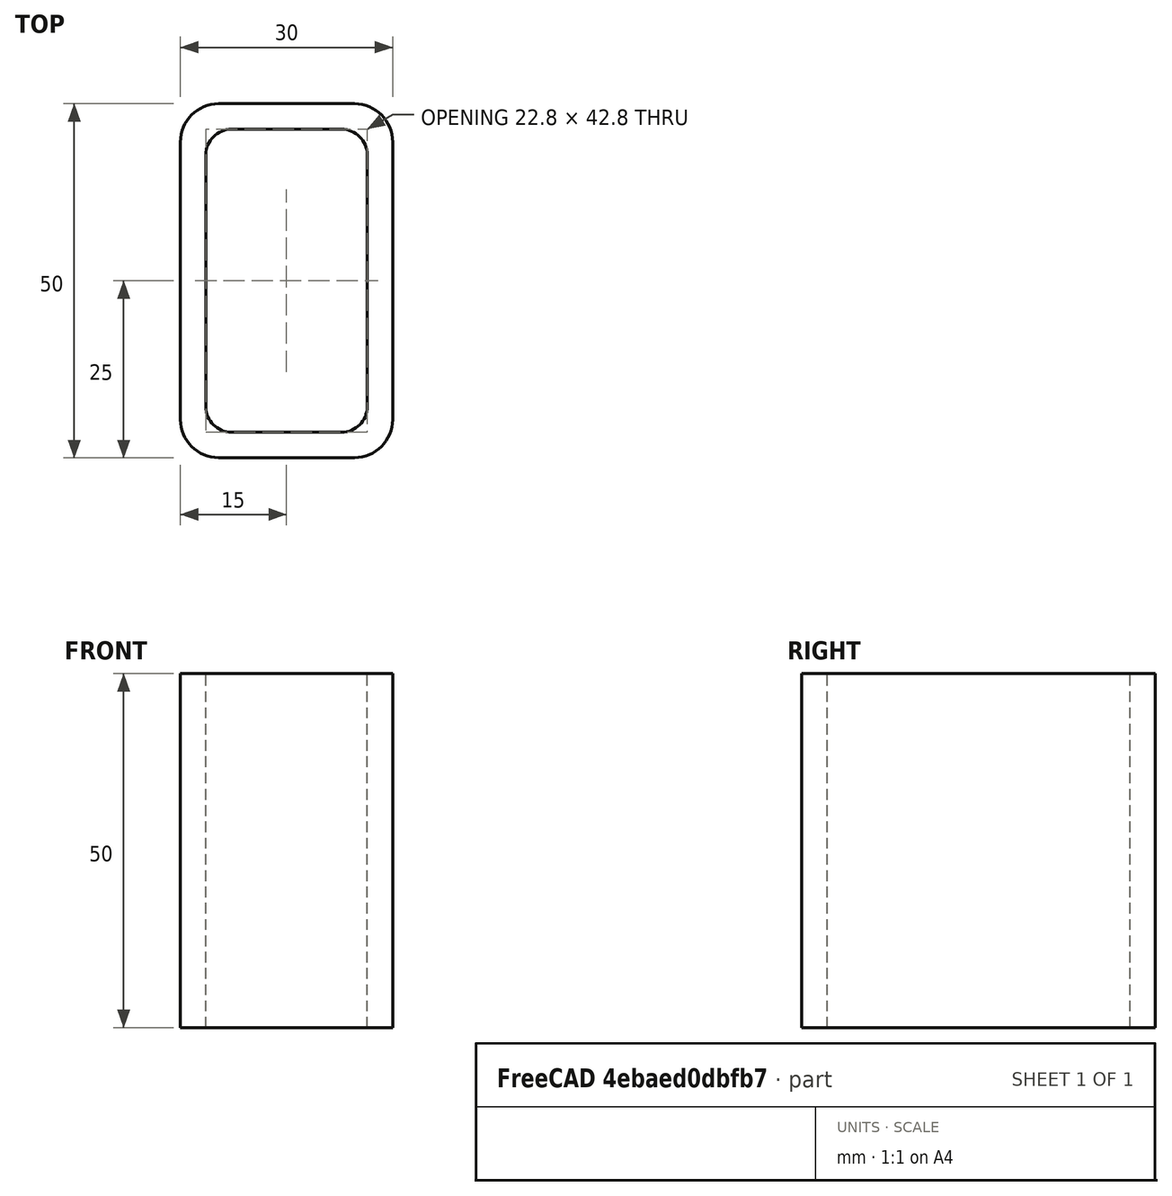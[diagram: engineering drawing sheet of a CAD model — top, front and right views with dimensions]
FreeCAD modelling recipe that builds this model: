
FCSTD DOCUMENT  (FreeCAD 0.15R4671 (Git))
Label: Rectangular hollow section 50x30x3.6 EN10219 S235JRH
License: All rights reserved
LicenseURL: http://en.wikipedia.org/wiki/All_rights_reserved
objects: Sketcher::SketchObject×1, Part::Extrusion×1
note: 2 computed .brp shape members not serialized (recipe doc carries the construction recipe); baked Part::Feature solids carry a one-line shape summary decoded from their .brp

FEATURE [Sketcher::SketchObject] Sketch
  sketch-geometry (16):
    g0: LineSegment StartX=-7.8 StartY=21.4 StartZ=0 EndX=7.8 EndY=21.4 EndZ=0
    g1: LineSegment StartX=11.4 StartY=17.8 StartZ=0 EndX=11.4 EndY=-17.8 EndZ=0
    g2: LineSegment StartX=7.8 StartY=-21.4 StartZ=0 EndX=-7.8 EndY=-21.4 EndZ=0
    g3: LineSegment StartX=-11.4 StartY=-17.8 StartZ=0 EndX=-11.4 EndY=17.8 EndZ=0
    g4: LineSegment StartX=-9.6 StartY=25 StartZ=0 EndX=9.6 EndY=25 EndZ=0
    g5: LineSegment StartX=15 StartY=19.6 StartZ=0 EndX=15 EndY=-19.6 EndZ=0
    g6: LineSegment StartX=9.6 StartY=-25 StartZ=0 EndX=-9.6 EndY=-25 EndZ=0
    g7: LineSegment StartX=-15 StartY=-19.6 StartZ=0 EndX=-15 EndY=19.6 EndZ=0
    g8: ArcOfCircle CenterX=-7.8 CenterY=17.8 CenterZ=0 NormalX=0 NormalY=0 NormalZ=1 Radius=3.6 StartAngle=1.5708 EndAngle=3.14159
    g9: ArcOfCircle CenterX=7.8 CenterY=17.8 CenterZ=0 NormalX=0 NormalY=0 NormalZ=1 Radius=3.6 StartAngle=0 EndAngle=1.5708
    g10: ArcOfCircle CenterX=7.8 CenterY=-17.8 CenterZ=0 NormalX=0 NormalY=0 NormalZ=1 Radius=3.6 StartAngle=4.71239 EndAngle=6.28319
    g11: ArcOfCircle CenterX=-7.8 CenterY=-17.8 CenterZ=0 NormalX=0 NormalY=0 NormalZ=1 Radius=3.6 StartAngle=3.14159 EndAngle=4.71239
    g12: ArcOfCircle CenterX=9.6 CenterY=19.6 CenterZ=0 NormalX=0 NormalY=0 NormalZ=1 Radius=5.4 StartAngle=0 EndAngle=1.5708
    g13: ArcOfCircle CenterX=9.6 CenterY=-19.6 CenterZ=0 NormalX=0 NormalY=0 NormalZ=1 Radius=5.4 StartAngle=4.71239 EndAngle=6.28319
    g14: ArcOfCircle CenterX=-9.6 CenterY=-19.6 CenterZ=0 NormalX=0 NormalY=0 NormalZ=1 Radius=5.4 StartAngle=3.14159 EndAngle=4.71239
    g15: ArcOfCircle CenterX=-9.6 CenterY=19.6 CenterZ=0 NormalX=0 NormalY=0 NormalZ=1 Radius=5.4 StartAngle=1.5708 EndAngle=3.14159
  constraints (36):
    c: Horizontal(g2)
    c: Vertical(g3)
    c: Horizontal(g6)
    c: Vertical(g7)
    c: Tangent(g3,g8) = 1.5708
    c: Tangent(g0,g8) = 1.5708
    c: Tangent(g0,g9) = 1.5708
    c: Tangent(g1,g9) = 1.5708
    c: Tangent(g1,g10) = 1.5708
    c: Tangent(g2,g10) = 1.5708
    c: Tangent(g2,g11) = 1.5708
    c: Tangent(g3,g11) = 1.5708
    c: Tangent(g4,g12) = 1.5708
    c: Tangent(g5,g12) = 1.5708
    c: Tangent(g5,g13) = 1.5708
    c: Tangent(g6,g13) = 1.5708
    c: Tangent(g6,g14) = 1.5708
    c: Tangent(g7,g14) = 1.5708
    c: Tangent(g7,g15) = 1.5708
    c: Tangent(g4,g15) = 1.5708
    c: Equal(g9,g8)
    c: Equal(g9,g11)
    c: Equal(g9,g10)
    c: Equal(g12,g15)
    c: Equal(g12,g14)
    c: Equal(g12,g13)
    c: Symmetric(g4,g6,g-1)
    c: Symmetric(g7,g5,g-2)
    c: DistanceY(g4,g6) = -50
    c: DistanceX(g7,g5) = 30
    c: Symmetric(g3,g1,g-2)
    c: Symmetric(g0,g2,g-1)
    c: DistanceY(g0,g4) = 3.6
    c: DistanceX(g5,g1) = -3.6
    c: Radius(g9) = 3.6
    c: Radius(g12) = 5.4
FEATURE [Part::Extrusion] Extrude  label="Rectangular hollow section 50x30x3.6 EN10219 S235JRH"
  Base = -> Sketch
  Dir = (0,0,50)
  Solid = true
